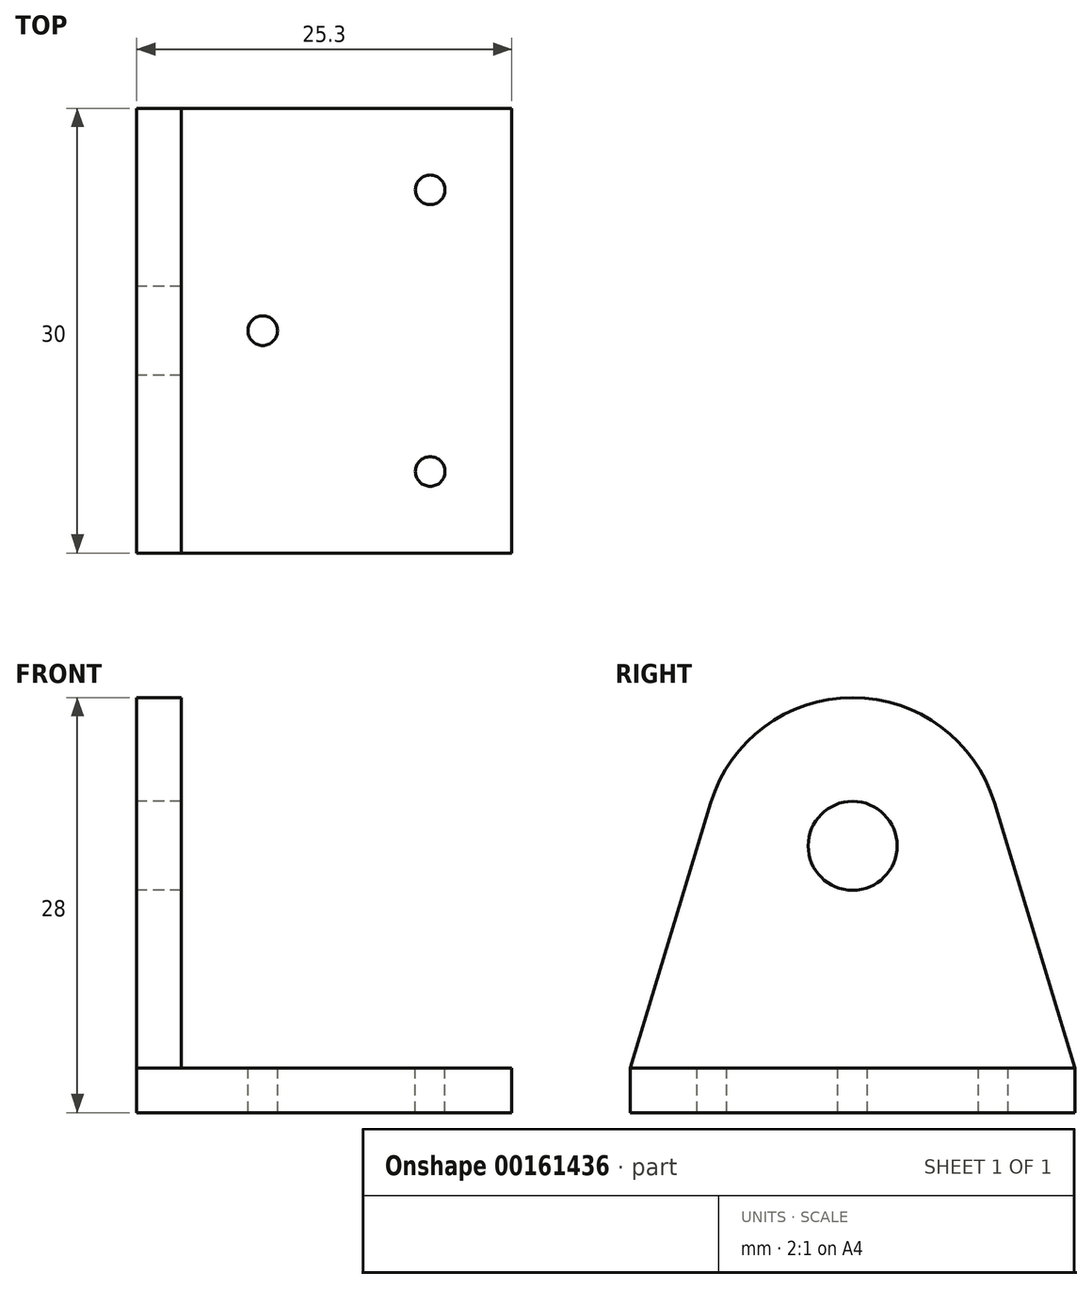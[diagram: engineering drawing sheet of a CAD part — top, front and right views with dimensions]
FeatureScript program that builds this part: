
annotation { "Feature Type Name" : "Feature", "Feature Type Description" : "" }
export const myFeature = defineFeature(function(context is Context, id is Id, definition is map)
    precondition{}
    {
        {
            var Q0;
            Q0=qCreatedBy(makeId("Top.planeOp"),FACE);
            var sketch = newSketch(context, id + "F0", { "sketchPlane" : qUnion([Q0])});
            skLineSegment(sketch, "E0.bottom", {"start": v(12.65, 15) * mm, "end": v(-12.65, 15) * mm});
            skLineSegment(sketch, "E0.top", {"start": v(12.65, -15) * mm, "end": v(-12.65, -15) * mm});
            skLineSegment(sketch, "E0.left", {"start": v(12.65, 15) * mm, "end": v(12.65, -15) * mm});
            skLineSegment(sketch, "E0.right", {"start": v(-12.65, 15) * mm, "end": v(-12.65, -15) * mm});
            skPoint(sketch, "E0.middle", {"position": v(0, 0) * mm});
            skSolve(sketch);
        }
        {
            var Q0;
            Q0 = qSketchRegion(id + "F0", true);
            extrude(context, id + "F1", {"entities" : qUnion([Q0]), "oppositeDirection" : true, "depth" : 3 * mm});
        }
        {
            var Q0;
            Q0=makeQuery(id+"F1.opExtrude","CAP_FACE",FACE,{"disambiguationData":[OSD([sQuery(id+"F0.wireOp",EDGE,"E0.bottom"),sQuery(id+"F0.wireOp",EDGE,"E0.top"),sQuery(id+"F0.wireOp",EDGE,"E0.left"),sQuery(id+"F0.wireOp",EDGE,"E0.right")])],"isStart":true});
            var sketch = newSketch(context, id + "F2", { "sketchPlane" : qUnion([Q0])});
            skLineSegment(sketch, "E1.bottom", {"start": v(-12.65, 15) * mm, "end": v(-9.65, 15) * mm});
            skLineSegment(sketch, "E1.top", {"start": v(-12.65, -15) * mm, "end": v(-9.65, -15) * mm});
            skLineSegment(sketch, "E1.left", {"start": v(-12.65, 15) * mm, "end": v(-12.65, -15) * mm});
            skLineSegment(sketch, "E1.right", {"start": v(-9.65, 15) * mm, "end": v(-9.65, -15) * mm});
            skSolve(sketch);
        }
        {
            var Q0;
            Q0 = qSketchRegion(id + "F2", true);
            var Q1;
            Q1 = qSketchRegion(id + "F4", true);
            extrude(context, id + "F3", {"entities" : qUnion([Q0, Q1]), "operationType" : NewBodyOperationType.ADD, "depth" : 25 * mm});
        }
        {
            var Q0;
            Q0=makeQuery(id+"F3.boolean.opBoolean","MERGE",FACE,{"derivedFrom":[makeQuery(id+"F1.opExtrude","SWEPT_FACE",FACE,{"disambiguationData":[OSD([sQuery(id+"F0.wireOp",EDGE,"E0.right")])]}),makeQuery(id+"F3.opExtrude","SWEPT_FACE",FACE,{"disambiguationData":[OSD([sQuery(id+"F2.wireOp",EDGE,"E1.left")])]})]});
            var sketch = newSketch(context, id + "F4", { "sketchPlane" : qUnion([Q0])});
            skLineSegment(sketch, "E2", {"start": v(0, -3) * mm, "end": v(0, 15) * mm});
            skPoint(sketch, "E2.endSnap0", {"position": v(0, -3) * mm});
            skCircle(sketch, "E3", {"center": v(0, 15) * mm, "radius": 3 * mm});
            skArc(sketch, "E4", {"start": v(9.57, 17.9) * mm, "mid": v(0, 25) * mm, "end": v(-9.57, 17.9) * mm});
            skLineSegment(sketch, "E5", {"start": v(-15, 0) * mm, "end": v(-9.57, 17.9) * mm});
            skLineSegment(sketch, "E6", {"start": v(15, 0) * mm, "end": v(9.57, 17.9) * mm});
            skSolve(sketch);
        }
        {
            var Q0;
            Q0=makeQuery(id+"F4.imprint","IMPRINT",FACE,{"disambiguationData":[TD([[makeQuery(id+"F4.imprint","IMPRINT",EDGE,{"derivedFrom":sQuery(id+"F4.wireOp",EDGE,"E3")}),1.0]])]});
            var Q1;
            {var subQ0=sQuery(id+"F4.wireOp",EDGE,"E5");Q1=makeQuery(id+"F4.imprint","IMPRINT",FACE,{"disambiguationData":[TD([[makeQuery(id+"F4.imprint","IMPRINT",EDGE,{"derivedFrom":subQ0}),1.0]])]});}
            var Q2;
            {var subQ0=sQuery(id+"F4.wireOp",EDGE,"E6");Q2=makeQuery(id+"F4.imprint","IMPRINT",FACE,{"disambiguationData":[TD([[makeQuery(id+"F4.imprint","IMPRINT",EDGE,{"derivedFrom":subQ0}),-1.0]])]});}
            extrude(context, id + "F5", {"entities" : qUnion([Q0, Q1, Q2]), "operationType" : NewBodyOperationType.REMOVE, "oppositeDirection" : true, "depth" : 3 * mm});
        }
        {
            var Q0;
            Q0=makeQuery(id+"F1.opExtrude","CAP_FACE",FACE,{"disambiguationData":[OSD([sQuery(id+"F0.wireOp",EDGE,"E0.bottom"),sQuery(id+"F0.wireOp",EDGE,"E0.top"),sQuery(id+"F0.wireOp",EDGE,"E0.left"),sQuery(id+"F0.wireOp",EDGE,"E0.right")])],"isStart":true});
            var sketch = newSketch(context, id + "F6", { "sketchPlane" : qUnion([Q0])});
            skPoint(sketch, "E7.endSnap0", {"position": v(-9.65, 0) * mm});
            skCircle(sketch, "E8", {"center": v(-4.15, 0) * mm, "radius": 1 * mm});
            skCircle(sketch, "E9", {"center": v(7.15, 9.5) * mm, "radius": 1 * mm});
            skCircle(sketch, "E10", {"center": v(7.15, -9.5) * mm, "radius": 1 * mm});
            skSolve(sketch);
        }
        {
            var Q0;
            Q0=makeQuery(id+"F6.imprint","IMPRINT",FACE,{"disambiguationData":[TD([[makeQuery(id+"F6.imprint","IMPRINT",EDGE,{"derivedFrom":sQuery(id+"F6.wireOp",EDGE,"E10")}),1.0]])]});
            var Q1;
            Q1=makeQuery(id+"F6.imprint","IMPRINT",FACE,{"disambiguationData":[TD([[makeQuery(id+"F6.imprint","IMPRINT",EDGE,{"derivedFrom":sQuery(id+"F6.wireOp",EDGE,"E8")}),1.0]])]});
            var Q2;
            Q2=makeQuery(id+"F6.imprint","IMPRINT",FACE,{"disambiguationData":[TD([[makeQuery(id+"F6.imprint","IMPRINT",EDGE,{"derivedFrom":sQuery(id+"F6.wireOp",EDGE,"E9")}),1.0]])]});
            extrude(context, id + "F7", {"entities" : qUnion([Q0, Q1, Q2]), "operationType" : NewBodyOperationType.REMOVE, "oppositeDirection" : true, "depth" : 3 * mm});
        }
    });
